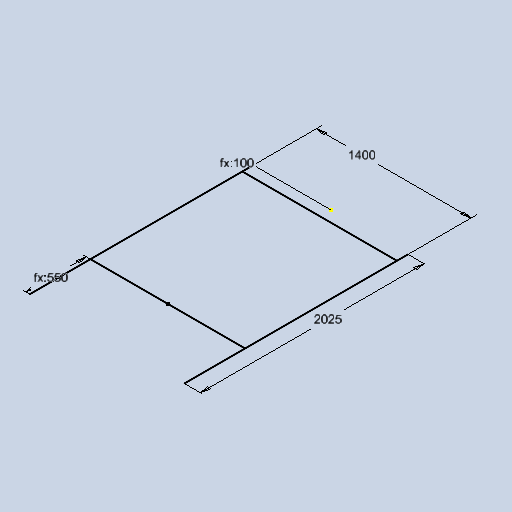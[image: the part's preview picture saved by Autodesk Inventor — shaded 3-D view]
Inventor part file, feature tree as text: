
AUTODESK INVENTOR PART (.ipt)
format: ipt  version: 2025 (Build 290162010, 162A)  size: 260,096 bytes
history: native  units: in
note: dims shown in document units (in); Inventor stores cm internally (conversion verified against a paired STEP export)
features: sketch x1
ambient origin geometry x8: Origin, YZ Plane, XZ Plane, XY Plane, X Axis, Y Axis, Z Axis, Center Point
feature tree (1):
  sketch  "Sketch3"  dims[d7=55.1181in d9=79.7244in d11=21.6535in d12=3.937in]
